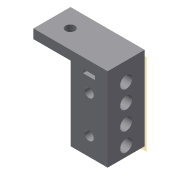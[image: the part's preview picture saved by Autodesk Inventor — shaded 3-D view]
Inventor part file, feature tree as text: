
AUTODESK INVENTOR PART (.ipt)
format: ipt  version: 2019.4 (Build 234330000, 330)  size: 162,304 bytes
history: native  units: mm
features: sketch x4, extrude x3, reference x3, projected_geometry x3, other x3, plane x2, hole x1
ambient origin geometry x8: Origin, YZ Plane, XZ Plane, XY Plane, X Axis, Y Axis, Z Axis, Center Point
bodies: Solid1 (feature_tree)
feature tree (19):
  plane  "Work Plane1"
  sketch  "Sketch1"  dims[d0=40.0mm d1=5.0mm]
  plane  "Work Plane2"
  extrude  "Extrusion1"  Depth=5.0mm
  hole  "Hole1"  [1 undecoded]
  extrude  "Extrusion2"  Depth=10.0mm
  extrude  "Extrusion3"  Depth=40.0mm
  reference  "Reference1"
  sketch  "Sketch2"  dims[d2=10.0mm d3=0.0mm d5=2.8mm]
  projected_geometry  "Projected Loop1"
  reference  "Reference2"
  reference  "Reference3"
  projected_geometry  "Projected Loop2"
  sketch  "Sketch3"  dims[d6=20.0mm d8=10.0mm d9=10.0mm d11=10.0mm d13=2.8mm]
  projected_geometry  "Projected Loop3"
  sketch  "Sketch5"  dims[d14=10.0mm d15=2.8mm d16=6.0mm d17=6.5mm d18=7.0mm d19=90.0deg d20=8.0mm d21=20.594885mm d22=40.0mm d23=5.0mm d24=5.0mm d25=0.0mm d33=6.5mm d34=2.0mm d35=10.0mm d36=0.0mm d37=1.0mm d38=1.0mm d39=1.0mm d40=0.15mm d41=0.25mm d42=0.375mm d43=14.3117mm d44=0.75mm d45=20.594885mm d46=0.0625mm d47=0.75mm d48=0.375mm]
  other  "Assembly_neje_slide_y_wellplateholder_20mmrod.iam"
  other  "Neje_Base_Rod_double_20mm:1"
  other  "Neje_Base_Rod_20mm:2"
note: 1 required parameter value undecoded (feature->parameter linkage not recoverable at this tier; creation-order binding heuristic only, values carry confidence <= 0.55)
